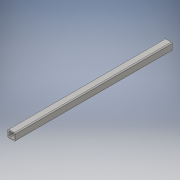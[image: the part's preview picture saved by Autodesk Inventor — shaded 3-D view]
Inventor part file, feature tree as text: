
AUTODESK INVENTOR PART (.ipt)
format: ipt  version: 2016 (Build 200138000, 138)  size: 113,664 bytes
history: native  units: in
note: dims shown in document units (in); Inventor stores cm internally (conversion verified against a paired STEP export)
features: extrude x1, sketch x1
ambient origin geometry x8: Origin, YZ Plane, XZ Plane, XY Plane, X Axis, Y Axis, Z Axis, Center Point
bodies: Solid1 (feature_tree)
feature tree (2):
  extrude  "Extrusion1"  Depth=1.0in
  sketch  "Sketch1"  dims[d0=1.0in d1=1.0in d2=0.125in d3=0.125in d4=21.0in d5=0.0in]
